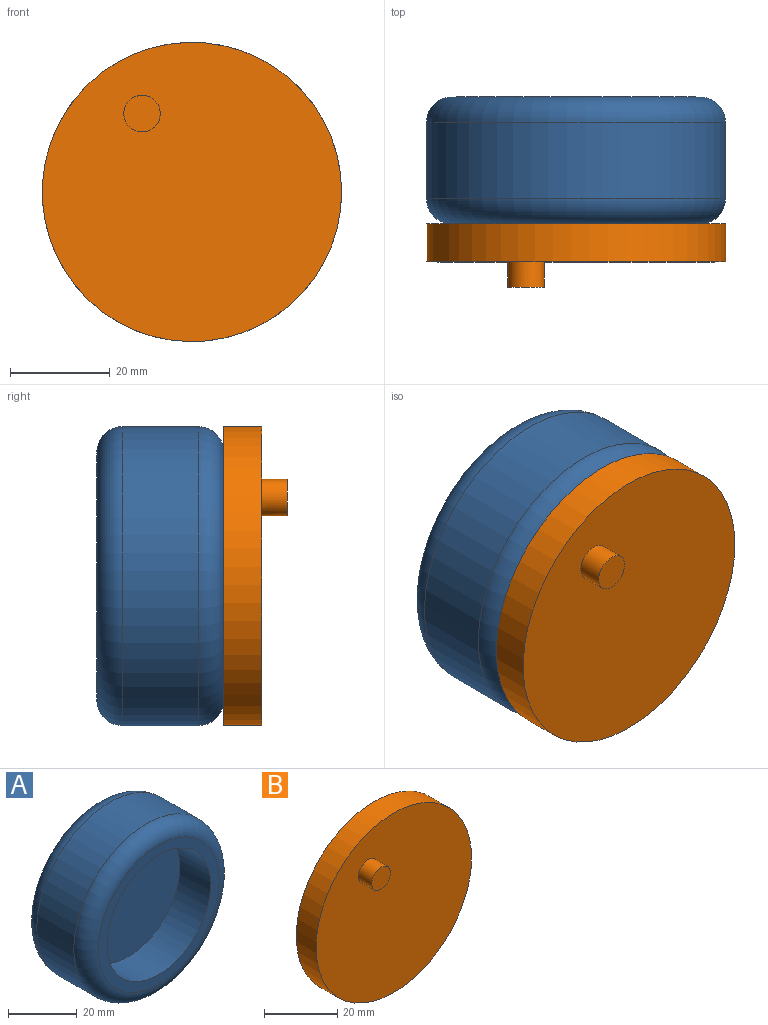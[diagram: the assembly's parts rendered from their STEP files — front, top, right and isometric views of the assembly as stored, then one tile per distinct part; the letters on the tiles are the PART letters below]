
ASSEMBLY  parts=2 mates=1
PART A: 7 faces, bbox 64.9x25.4x64.9 mm
  f0: cylinder r=29.97mm len=59.94mm, axis (0,1,0), area 2869.6mm2, adj f3,f4
  f1: plane 49.78x49.78mm, normal (0,-1,0), area 512.7mm2, adj f4,f5
  f2: plane 49.78x49.78mm, normal (0,1,0), area 1945.9mm2, adj f3
  f3: torus R=24.89mm, axis (0,-1,0), area 1409.9mm2, adj f0,f2
  f4: torus R=24.89mm, axis (0,-1,0), area 1409.9mm2, adj f0,f1
  f5: cylinder r=21.36mm len=42.72mm, axis (0,-1,0), area 1704.4mm2, adj f1,f6
  f6: plane 42.72x42.72mm, normal (0,-1,0), area 1433.2mm2, adj f5
PART B: 5 faces, bbox 59.9x12.7x59.9 mm
  f0: cylinder r=29.97mm len=59.94mm, axis (0,1,0), area 1435mm2, adj f1,f2
  f1: plane 59.94x59.94mm, normal (0,-1,0), area 2780.1mm2, adj f0,f3
  f2: plane 59.94x59.94mm, normal (0,1,0), area 2822.2mm2, adj f0
  f3: cylinder r=3.66mm len=7.31mm, axis (0,1,0), area 116.7mm2, adj f1,f4
  f4: plane 7.31x7.31mm, normal (0,-1,0), area 42mm2, adj f3
PLACE A t=(-18.91,4.83,-0.76)mm
PLACE B t=(-18.91,-20.57,-0.76)mm
MATE revolute B.f0 <-> A.f0  axis (0,1,0) through (-18.91,-20.57,-0.76)mm
